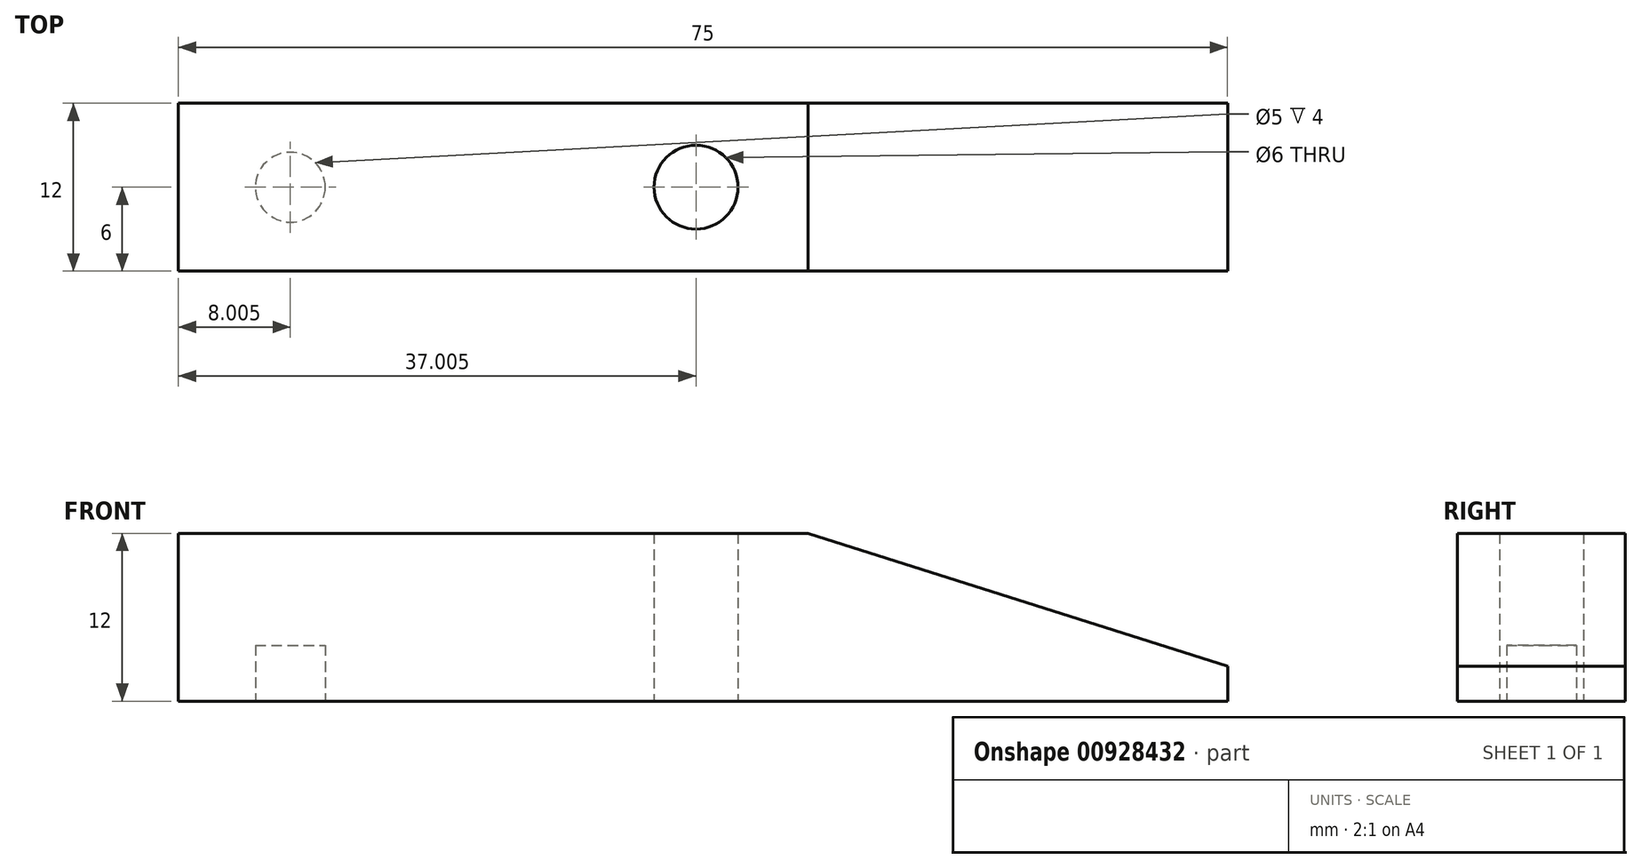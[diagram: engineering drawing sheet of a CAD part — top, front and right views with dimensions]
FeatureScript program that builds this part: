
annotation { "Feature Type Name" : "Feature", "Feature Type Description" : "" }
export const myFeature = defineFeature(function(context is Context, id is Id, definition is map)
    precondition{}
    {
        {
            var Q0;
            Q0=qCreatedBy(makeId("Front.planeOp"),FACE);
            var sketch = newSketch(context, id + "F0", { "sketchPlane" : qUnion([Q0])});
            skLineSegment(sketch, "E0", {"start": v(-26, 9.5) * mm, "end": v(19, 9.5) * mm});
            skLineSegment(sketch, "E1", {"start": v(19, 9.5) * mm, "end": v(49, 0) * mm});
            skLineSegment(sketch, "E2", {"start": v(49, -2.5) * mm, "end": v(-26, -2.5) * mm});
            skLineSegment(sketch, "E3", {"start": v(-26, 9.5) * mm, "end": v(-26, -2.5) * mm});
            skLineSegment(sketch, "E4", {"start": v(49, 0) * mm, "end": v(49, -2.5) * mm});
            skSolve(sketch);
        }
        {
            var Q0;
            Q0=makeQuery(id+"F0.imprint","IMPRINT",FACE,{"disambiguationData":[TD([[makeQuery(id+"F0.imprint","IMPRINT",EDGE,{"derivedFrom":sQuery(id+"F0.wireOp",EDGE,"E0")}),-1.0]])]});
            extrude(context, id + "F1", {"entities" : qUnion([Q0]), "depth" : 12 * mm, "offsetDistance" : 25 * mm});
        }
        {
            var Q0;
            Q0=makeQuery(id+"F1.opExtrude","SWEPT_FACE",FACE,{"disambiguationData":[OSD([sQuery(id+"F0.wireOp",EDGE,"E2")])]});
            var sketch = newSketch(context, id + "F2", { "sketchPlane" : qUnion([Q0])});
            skCircle(sketch, "E5", {"center": v(-18, 6) * mm, "radius": 2.5 * mm});
            skSolve(sketch);
        }
        {
            var Q0;
            Q0=qSketchRegion(id+"F2",true);
            extrude(context, id + "F3", {"entities" : qUnion([Q0]), "operationType" : NewBodyOperationType.REMOVE, "oppositeDirection" : true, "depth" : 4 * mm, "offsetDistance" : 25 * mm});
        }
        {
            var Q0;
            Q0=makeQuery(id+"F1.opExtrude","SWEPT_FACE",FACE,{"disambiguationData":[OSD([sQuery(id+"F0.wireOp",EDGE,"E2")])]});
            var sketch = newSketch(context, id + "F4", { "sketchPlane" : qUnion([Q0])});
            skCircle(sketch, "E6", {"center": v(11, 6) * mm, "radius": 3 * mm});
            skSolve(sketch);
        }
        {
            var Q0;
            Q0=qSketchRegion(id+"F4",true);
            extrude(context, id + "F5", {"entities" : qUnion([Q0]), "operationType" : NewBodyOperationType.REMOVE, "oppositeDirection" : true, "depth" : 12 * mm, "offsetDistance" : 25 * mm});
        }
    });
